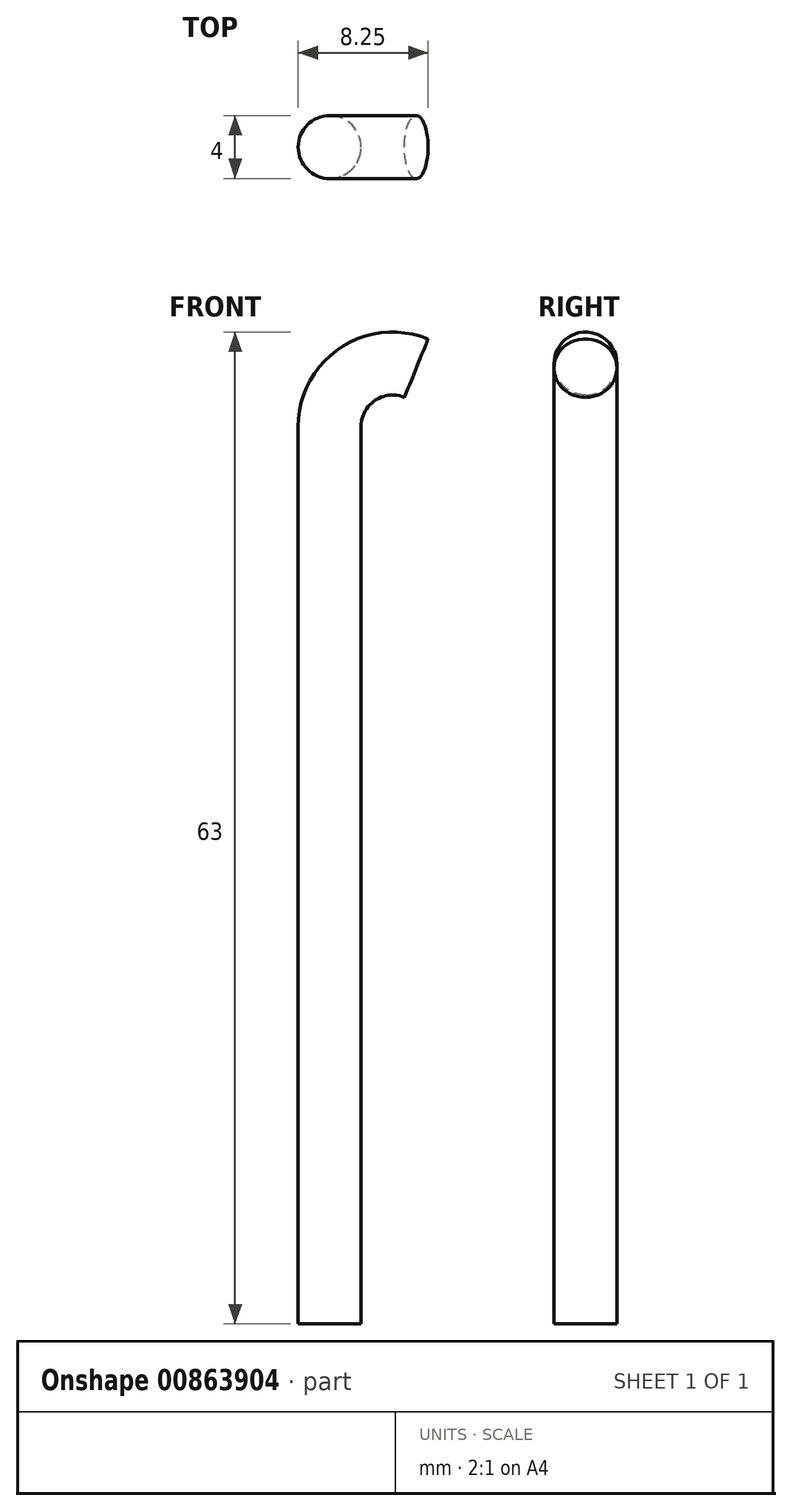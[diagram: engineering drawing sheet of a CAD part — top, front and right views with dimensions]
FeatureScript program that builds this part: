
annotation { "Feature Type Name" : "Feature", "Feature Type Description" : "" }
export const myFeature = defineFeature(function(context is Context, id is Id, definition is map)
    precondition{}
    {
        {
            var Q0;
            Q0=qCreatedBy(makeId("Front.planeOp"),FACE);
            var sketch = newSketch(context, id + "F0", { "sketchPlane" : qUnion([Q0])});
            skLineSegment(sketch, "E0", {"start": v(0, 0) * mm, "end": v(0, 57) * mm});
            skArc(sketch, "E1", {"start": v(5.5, 60.7) * mm, "mid": v(1.76, 60.32) * mm, "end": v(0, 57) * mm});
            skSolve(sketch);
        }
        {
            var Q0;
            Q0=qCreatedBy(makeId("Top.planeOp"),FACE);
            var sketch = newSketch(context, id + "F1", { "sketchPlane" : qUnion([Q0])});
            skCircle(sketch, "E2", {"center": v(0, 0) * mm, "radius": 2 * mm});
            skSolve(sketch);
        }
        {
            var Q0;
            Q0=makeQuery(id+"F1.imprint","IMPRINT",FACE,{"disambiguationData":[TD([[makeQuery(id+"F1.imprint","IMPRINT",EDGE,{"derivedFrom":sQuery(id+"F1.wireOp",EDGE,"E2")}),1.0]])]});
            var Q1;
            Q1=sQuery(id+"F0.wireOp",EDGE,"E0");
            var Q2;
            Q2=sQuery(id+"F0.wireOp",EDGE,"E1");
            sweep(context, id + "F2", {"profiles" : qUnion([Q0]), "path" : qUnion([Q1, Q2])});
        }
    });
